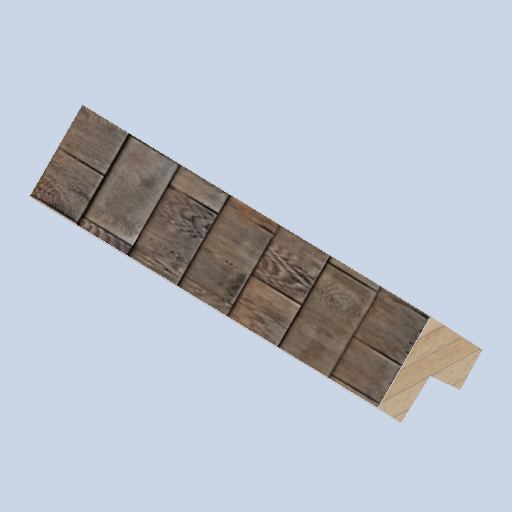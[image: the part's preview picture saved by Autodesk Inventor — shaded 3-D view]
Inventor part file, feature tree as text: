
AUTODESK INVENTOR PART (.ipt)
format: ipt  version: 2024.2 (Build 282272000, 272)  size: 240,128 bytes
history: native  units: in
note: dims shown in document units (in); Inventor stores cm internally (conversion verified against a paired STEP export)
features: sketch x8, plane x6, other x3
ambient origin geometry x8: Origin, YZ Plane, XZ Plane, XY Plane, X Axis, Y Axis, Z Axis, Center Point
bodies: Solid1 (feature_tree)
feature tree (17):
  other  "panel_pad_frame_01.ipt"
  other  "Solid1::panel_pad_frame_01.ipt"
  other  "TaggingFeature1"
  sketch  "Sketch1"  dims[d0=0.3937in]
  sketch  "Sketch2"
  sketch  "Sketch3"
  sketch  "Sketch6"
  sketch  "Sketch7"
  sketch  "Sketch8"
  sketch  "Sketch9"
  sketch  "Sketch10"
  plane  "Work Plane1"
  plane  "Work Plane2"
  plane  "Work Plane3"
  plane  "Work Plane4"
  plane  "Work Plane5"
  plane  "Work Plane6"
